# Revit family: NAR LED WALL PACK
name_source: partatom
category: Lighting Fixtures
units: mm (PartAtom-declared; Revit-internal decimal feet)

## family parameters
Always vertical = Yes
Cut with Voids When Loaded = No
Light Source = Yes
Maintain Annotation Orientation = No
OmniClass Number = 23.80.70.00
OmniClass Title = Lighting
Part Type = Normal
Room Calculation Point = No
Round Connector Dimension = Use Diameter
Shared = No
Work Plane-Based = No

## types (6) — shared parameters
CRI = 70
Color Filter = 16777215
Default Elevation = 3' - 0"
Dimming Lamp Color Temperature Shift = <None>
IP Rating = 65
Input Voltage = 120-277V
Lamp = LED
Load Classification = Lighting
Manufacturer = Above All Lighting
Power Factor = 0.9
Tilt Angle = 90.00°
URL = https://www.abovealllighting.com

## per-type parameters (varying)
| type | Bottom | Model | Photometric Web File | Top | Wattage Comments |
| NAR-80SP-40W-3000K | 0' - 6 1/2" | NAR-80SP-SW1-BK | NAR_80SP_SW1_BK__40W_3000K_.ies | 0' - 4 3/16" | 40W |
| NAR-80SP-60W-3000K | 0' - 6 1/2" | NAR-80SP-SW1-BK | NAR_80SP_SW1_BK__60W_3000K_.ies | 0' - 4 3/16" | 60W |
| NAR-80SP-80W-3000K | 0' - 6 1/2" | NAR-80SP-SW1-BK | NAR_80SP_SW1_BK__80W_3000K_.ies | 0' - 4 3/16" | 80W |
| NAR-150SP-100W-3000K | 0' - 9 19/32" | NAR-150SP-SW1-BK | NAR_80SP_SW1_BK__100W_3000K_.ies | 0' - 5" | 100W |
| NAR-150SP-120W-3000K | 0' - 9 19/32" | NAR-150SP-SW1-BK | NAR_80SP_SW1_BK__120W_3000K_.ies | 0' - 5" | 120W |
| NAR-150SP-150W-3000K | 0' - 9 19/32" | NAR-150SP-SW1-BK | NAR_80SP_SW1_BK__150W_3000K_.ies | 0' - 5" | 150W |

## geometry (parser evidence)
native form markers: Sweep x3
no freeform markers — native parametric forms only
